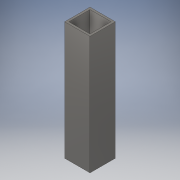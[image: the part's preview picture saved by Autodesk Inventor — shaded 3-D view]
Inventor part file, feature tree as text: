
AUTODESK INVENTOR PART (.ipt)
format: ipt  version: 2019 (Build 230136000, 136)  size: 102,912 bytes
history: native  units: mm
features: extrude x1, sketch x1
ambient origin geometry x8: Origin, YZ Plane, XZ Plane, XY Plane, X Axis, Y Axis, Z Axis, Center Point
bodies: Solid1 (feature_tree)
feature tree (2):
  extrude  "Extrusion1"  Depth=30.0mm
  sketch  "Sketch1"  dims[d0=30.0mm d1=30.0mm d2=2.5mm d3=2.5mm d4=140.0mm d5=0.0mm]
